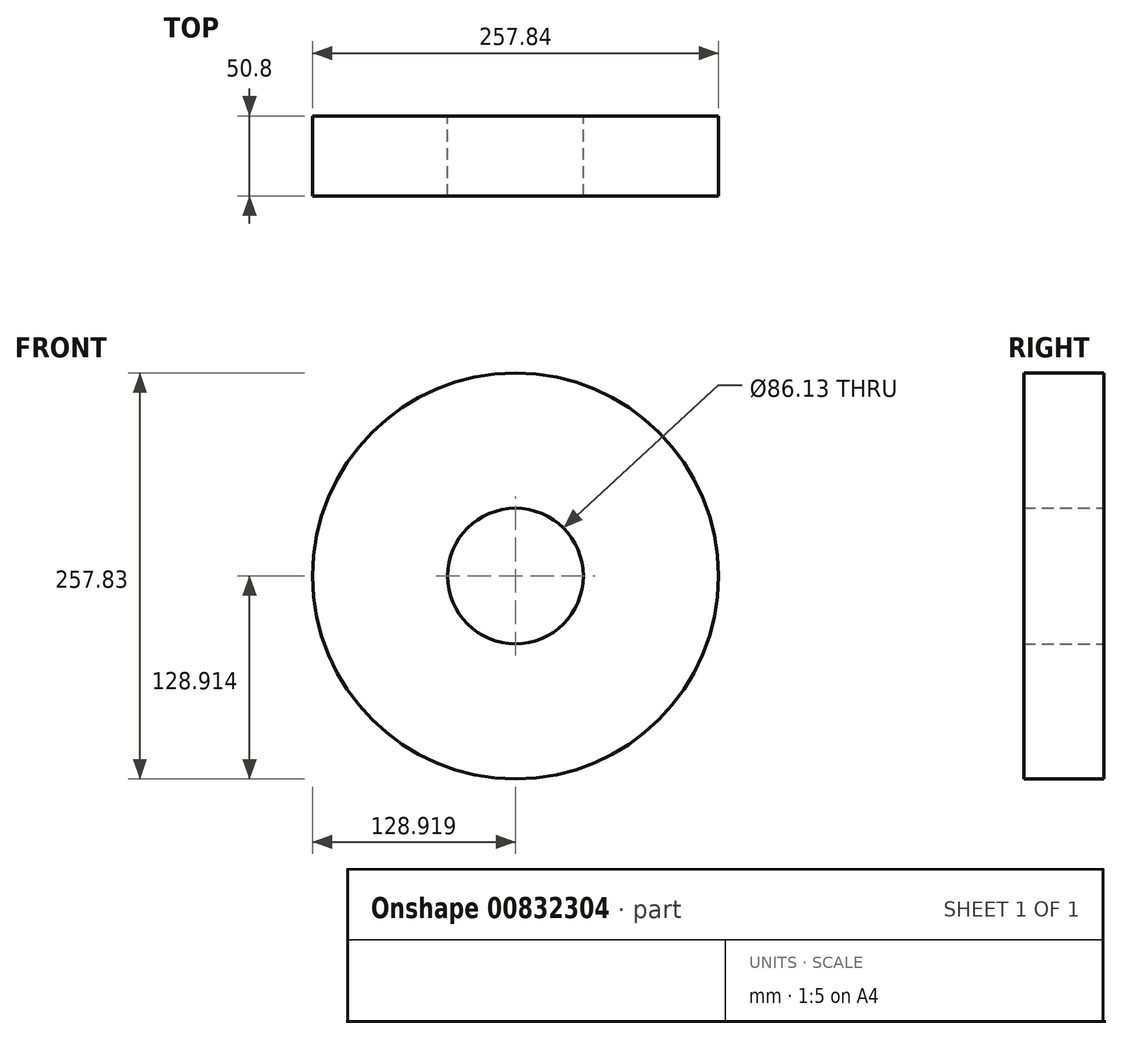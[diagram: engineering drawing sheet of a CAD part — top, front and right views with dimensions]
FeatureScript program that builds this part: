
annotation { "Feature Type Name" : "Feature", "Feature Type Description" : "" }
export const myFeature = defineFeature(function(context is Context, id is Id, definition is map)
    precondition{}
    {
        {
            var Q0;
            Q0=qCreatedBy(makeId("Front.planeOp"),FACE);
            var sketch = newSketch(context, id + "F0", { "sketchPlane" : qUnion([Q0])});
            skCircle(sketch, "E0", {"center": v(-411.7, 145.41) * mm, "radius": 128.92 * mm});
            skCircle(sketch, "E1", {"center": v(-411.7, 145.41) * mm, "radius": 43.06 * mm});
            skSolve(sketch);
        }
        {
            var Q0;
            Q0=makeQuery(id+"F0.imprint","IMPRINT",FACE,{"disambiguationData":[TD([[makeQuery(id+"F0.imprint","IMPRINT",EDGE,{"derivedFrom":sQuery(id+"F0.wireOp",EDGE,"E0")}),1.0]])]});
            extrude(context, id + "F1", {"entities" : qUnion([Q0]), "depth" : 50.8 * mm, "offsetDistance" : 25.4 * mm});
        }
    });
